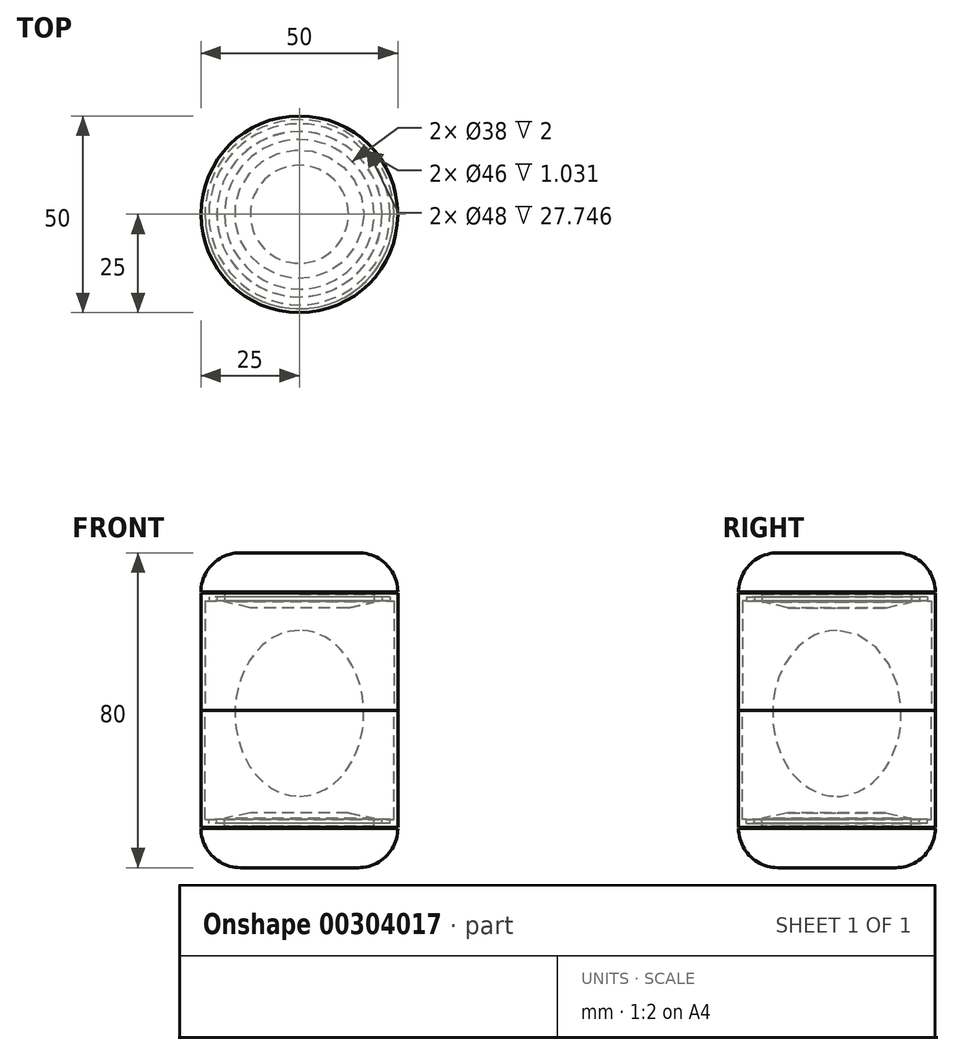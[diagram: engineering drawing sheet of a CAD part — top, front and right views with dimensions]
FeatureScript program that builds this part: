
annotation { "Feature Type Name" : "Feature", "Feature Type Description" : "" }
export const myFeature = defineFeature(function(context is Context, id is Id, definition is map)
    precondition{}
    {
        {
            var Q0;
            Q0=qCreatedBy(makeId("Front.planeOp"),FACE);
            var sketch = newSketch(context, id + "F0", { "sketchPlane" : qUnion([Q0])});
            skLineSegment(sketch, "E0", {"start": v(0, 0) * mm, "end": v(0, 10) * mm});
            skLineSegment(sketch, "E1", {"start": v(0, 10) * mm, "end": v(-26, 10) * mm});
            skLineSegment(sketch, "E2", {"start": v(-25, 10) * mm, "end": v(-26, 10) * mm});
            skLineSegment(sketch, "E3", {"start": v(0, 0) * mm, "end": v(-15, 0) * mm});
            skArc(sketch, "E4", {"start": v(-15, 0) * mm, "mid": v(-22.07, 2.93) * mm, "end": v(-25, 10) * mm});
            skSolve(sketch);
        }
        {
            var Q0;
            Q0=makeQuery(id+"F0.imprint","IMPRINT",FACE,{"disambiguationData":[TD([[makeQuery(id+"F0.imprint","IMPRINT",EDGE,{"derivedFrom":sQuery(id+"F0.wireOp",EDGE,"E0")}),1.0]])]});
            var Q1;
            Q1=sQuery(id+"F0.wireOp",EDGE,"E0");
            revolve(context, id + "F1", {"entities" : qUnion([Q0]), "axis" : qUnion([Q1]), "revolveType" : RevolveType.FULL});
        }
        {
            var Q0;
            Q0=qCreatedBy(makeId("Front.planeOp"),FACE);
            var sketch = newSketch(context, id + "F2", { "sketchPlane" : qUnion([Q0])});
            skLineSegment(sketch, "E5", {"start": v(-25, 10.25) * mm, "end": v(-25, 12.25) * mm});
            skLineSegment(sketch, "E6", {"start": v(-25, 12.25) * mm, "end": v(-23, 12.25) * mm});
            skLineSegment(sketch, "E7", {"start": v(-21, 12.25) * mm, "end": v(-19, 12.25) * mm});
            skLineSegment(sketch, "E8", {"start": v(-19, 12.25) * mm, "end": v(-19, 10.25) * mm});
            skLineSegment(sketch, "E9", {"start": v(-23, 12.25) * mm, "end": v(-23, 11.22) * mm});
            skLineSegment(sketch, "E10", {"start": v(-23, 11.22) * mm, "end": v(-20.97, 11.22) * mm});
            skLineSegment(sketch, "E11", {"start": v(-20.97, 11.22) * mm, "end": v(-21, 12.25) * mm});
            skLineSegment(sketch, "E12", {"start": v(-25, 10.25) * mm, "end": v(-19, 10.25) * mm});
            skLineSegment(sketch, "E13", {"start": v(0, 23.72) * mm, "end": v(0, -18.22) * mm, "construction": true});
            skSolve(sketch);
        }
        {
            var Q0;
            Q0=makeQuery(id+"F2.imprint","IMPRINT",FACE,{"disambiguationData":[TD([[makeQuery(id+"F2.imprint","IMPRINT",EDGE,{"derivedFrom":sQuery(id+"F2.wireOp",EDGE,"E5")}),-1.0]])]});
            var Q1;
            Q1=sQuery(id+"F2.wireOp",EDGE,"E13");
            revolve(context, id + "F3", {"entities" : qUnion([Q0]), "axis" : qUnion([Q1]), "revolveType" : RevolveType.FULL});
        }
        {
            var Q0;
            Q0=qCreatedBy(makeId("Front.planeOp"),FACE);
            var sketch = newSketch(context, id + "F4", { "sketchPlane" : qUnion([Q0])});
            skLineSegment(sketch, "E14", {"start": v(-19, 10.51) * mm, "end": v(-19, 12.51) * mm});
            skLineSegment(sketch, "E15", {"start": v(-19, 12.51) * mm, "end": v(-12.44, 13.97) * mm});
            skLineSegment(sketch, "E16", {"start": v(-12.44, 13.97) * mm, "end": v(0, 13.97) * mm});
            skLineSegment(sketch, "E17", {"start": v(0, 13.97) * mm, "end": v(0, 10.47) * mm});
            skLineSegment(sketch, "E18", {"start": v(-19, 10.51) * mm, "end": v(0, 10.47) * mm});
            skSolve(sketch);
        }
        {
            var Q0;
            Q0=makeQuery(id+"F4.imprint","IMPRINT",FACE,{"disambiguationData":[TD([[makeQuery(id+"F4.imprint","IMPRINT",EDGE,{"derivedFrom":sQuery(id+"F4.wireOp",EDGE,"E14")}),-1.0]])]});
            var Q1;
            Q1=sQuery(id+"F4.wireOp",EDGE,"E17");
            revolve(context, id + "F5", {"entities" : qUnion([Q0]), "axis" : qUnion([Q1]), "revolveType" : RevolveType.FULL});
        }
        {
            var Q0;
            Q0=qCreatedBy(makeId("Front.planeOp"),FACE);
            var sketch = newSketch(context, id + "F6", { "sketchPlane" : qUnion([Q0])});
            skLineSegment(sketch, "E19", {"start": v(-25, 12) * mm, "end": v(-25, 40) * mm});
            skLineSegment(sketch, "E20", {"start": v(-25, 40) * mm, "end": v(-24, 40) * mm});
            skLineSegment(sketch, "E21", {"start": v(-24, 40) * mm, "end": v(-24, 12) * mm});
            skLineSegment(sketch, "E22", {"start": v(-24, 12) * mm, "end": v(-25, 12) * mm});
            skLineSegment(sketch, "E23", {"start": v(0, 30.4) * mm, "end": v(0, -25.2) * mm, "construction": true});
            skSolve(sketch);
        }
        {
            var Q0;
            Q0=makeQuery(id+"F6.imprint","IMPRINT",FACE,{"disambiguationData":[TD([[makeQuery(id+"F6.imprint","IMPRINT",EDGE,{"derivedFrom":sQuery(id+"F6.wireOp",EDGE,"E19")}),-1.0]])]});
            var Q1;
            Q1=sQuery(id+"F6.wireOp",EDGE,"E23");
            revolve(context, id + "F7", {"operationType" : NewBodyOperationType.ADD, "entities" : qUnion([Q0]), "axis" : qUnion([Q1]), "revolveType" : RevolveType.FULL});
        }
        {
            var Q0;
            Q0=makeQuery(id+"F5.opRevolve","SWEPT_BODY",BODY,{"disambiguationData":[OSD([sQuery(id+"F4.wireOp",EDGE,"E14"),sQuery(id+"F4.wireOp",EDGE,"E15"),sQuery(id+"F4.wireOp",EDGE,"E16"),sQuery(id+"F4.wireOp",EDGE,"E17"),sQuery(id+"F4.wireOp",EDGE,"E18")])]});
            var Q1;
            Q1=makeQuery(id+"F1.opRevolve","SWEPT_BODY",BODY,{"disambiguationData":[OSD([sQuery(id+"F0.wireOp",EDGE,"E0"),sQuery(id+"F0.wireOp",EDGE,"E1"),sQuery(id+"F0.wireOp",EDGE,"E3"),sQuery(id+"F0.wireOp",EDGE,"E4")])]});
            var Q2;
            Q2=makeQuery(id+"F7.opRevolve","SWEPT_FACE",FACE,{"disambiguationData":[OSD([sQuery(id+"F6.wireOp",EDGE,"E20")])]});
            mirror(context, id + "F8", {"entities" : qUnion([Q0, Q1]), "mirrorPlane" : qUnion([Q2])});
        }
        {
            var Q0;
            Q0=makeQuery(id+"F3.opRevolve","SWEPT_BODY",BODY,{"disambiguationData":[OSD([sQuery(id+"F2.wireOp",EDGE,"E5"),sQuery(id+"F2.wireOp",EDGE,"E6"),sQuery(id+"F2.wireOp",EDGE,"E7"),sQuery(id+"F2.wireOp",EDGE,"E8"),sQuery(id+"F2.wireOp",EDGE,"E9"),sQuery(id+"F2.wireOp",EDGE,"E10"),sQuery(id+"F2.wireOp",EDGE,"E11"),sQuery(id+"F2.wireOp",EDGE,"E12")])]});
            var Q1;
            Q1=makeQuery(id+"F7.opRevolve","SWEPT_FACE",FACE,{"disambiguationData":[OSD([sQuery(id+"F6.wireOp",EDGE,"E20")])]});
            mirror(context, id + "F9", {"operationType" : NewBodyOperationType.ADD, "entities" : qUnion([Q0]), "mirrorPlane" : qUnion([Q1])});
        }
        {
            var Q0;
            Q0=qCreatedBy(makeId("Front.planeOp"),FACE);
            var sketch = newSketch(context, id + "F10", { "sketchPlane" : qUnion([Q0])});
            skEllipticalArc(sketch, "E24", {});
            skLineSegment(sketch, "E25", {"start": v(0, 60.32) * mm, "end": v(0, 18.1) * mm});
            const initialGuessF10  = {"E24": [0, 0.039210524410009384, 0, -1, 0.021108552813529968, 0.01637779325771011, 0, 3.141592653589793]};
            skSetInitialGuess(sketch, initialGuessF10);
            skSolve(sketch);
        }
        {
            var Q0;
            Q0=makeQuery(id+"F10.imprint","IMPRINT",FACE,{"disambiguationData":[TD([[makeQuery(id+"F10.imprint","IMPRINT",EDGE,{"derivedFrom":sQuery(id+"F10.wireOp",EDGE,"E24")}),1.0]])]});
            var Q1;
            Q1=sQuery(id+"F10.wireOp",EDGE,"E25");
            revolve(context, id + "F11", {"entities" : qUnion([Q0]), "axis" : qUnion([Q1]), "revolveType" : RevolveType.FULL});
        }
    });
